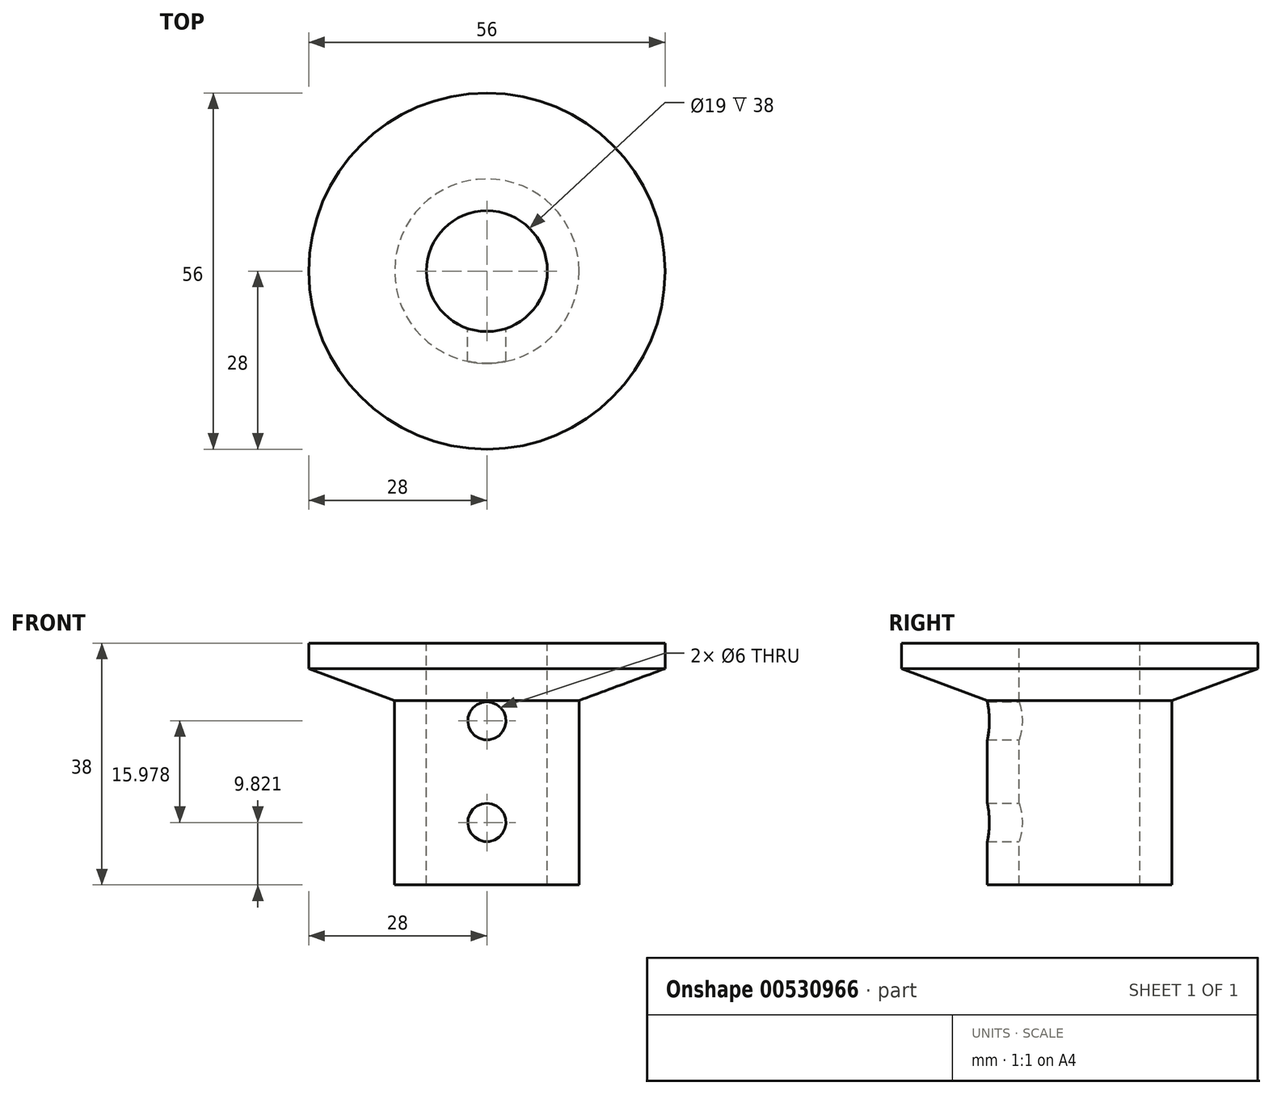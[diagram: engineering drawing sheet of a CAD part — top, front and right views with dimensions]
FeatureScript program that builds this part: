
annotation { "Feature Type Name" : "Feature", "Feature Type Description" : "" }
export const myFeature = defineFeature(function(context is Context, id is Id, definition is map)
    precondition{}
    {
        {
            var Q0;
            Q0=qCreatedBy(makeId("Front.planeOp"),FACE);
            var sketch = newSketch(context, id + "F0", { "sketchPlane" : qUnion([Q0])});
            skPoint(sketch, "E0.middle", {"position": v(0, 0) * mm});
            skLineSegment(sketch, "E1", {"start": v(-14.5, 11) * mm, "end": v(-28, 16) * mm});
            skLineSegment(sketch, "E2", {"start": v(-14.5, 11) * mm, "end": v(-14.5, -18) * mm});
            skLineSegment(sketch, "E3", {"start": v(0, 20) * mm, "end": v(-28, 20) * mm});
            skLineSegment(sketch, "E4", {"start": v(-28, 16) * mm, "end": v(-28, 16) * mm});
            skLineSegment(sketch, "E5", {"start": v(-28, 20) * mm, "end": v(-28, 16) * mm});
            skLineSegment(sketch, "E6", {"start": v(0, 20) * mm, "end": v(0, -18) * mm});
            skLineSegment(sketch, "E7", {"start": v(-14.5, -18) * mm, "end": v(0, -18) * mm});
            skSolve(sketch);
        }
        {
            var Q0;
            Q0=makeQuery(id+"F0.imprint","IMPRINT",FACE,{"disambiguationData":[TD([[makeQuery(id+"F0.imprint","IMPRINT",EDGE,{"derivedFrom":sQuery(id+"F0.wireOp",EDGE,"E1")}),-1.0]])]});
            var Q1;
            Q1=sQuery(id+"F0.wireOp",EDGE,"E6");
            revolve(context, id + "F1", {"entities" : qUnion([Q0]), "axis" : qUnion([Q1]), "revolveType" : RevolveType.SYMMETRIC, "angle" : 360 * degree});
        }
        {
            var Q0;
            Q0=qCreatedBy(makeId("Top.planeOp"),FACE);
            var sketch = newSketch(context, id + "F2", { "sketchPlane" : qUnion([Q0])});
            skCircle(sketch, "E8", {"center": v(0, 0) * mm, "radius": 9.5 * mm});
            skSolve(sketch);
        }
        {
            var Q0;
            Q0 = qSketchRegion(id + "F2", true);
            extrude(context, id + "F3", {"entities" : qUnion([Q0]), "operationType" : NewBodyOperationType.REMOVE, "endBound" : BoundingType.SYMMETRIC, "oppositeDirection" : true, "depth" : 100 * mm, "offsetDistance" : 25 * mm});
        }
        {
            var Q0;
            Q0=qCreatedBy(makeId("Front.planeOp"),FACE);
            var sketch = newSketch(context, id + "F4", { "sketchPlane" : qUnion([Q0])});
            skLineSegment(sketch, "E9", {"start": v(0, 16.82) * mm, "end": v(0, -8.18) * mm});
            skCircle(sketch, "E10", {"center": v(0, -8.18) * mm, "radius": 3 * mm});
            skCircle(sketch, "E11", {"center": v(0, 7.8) * mm, "radius": 3 * mm});
            skSolve(sketch);
        }
        {
            var Q0;
            Q0 = qSketchRegion(id + "F4", true);
            extrude(context, id + "F5", {"entities" : qUnion([Q0]), "operationType" : NewBodyOperationType.REMOVE, "depth" : 30 * mm, "offsetDistance" : 25 * mm});
        }
    });
